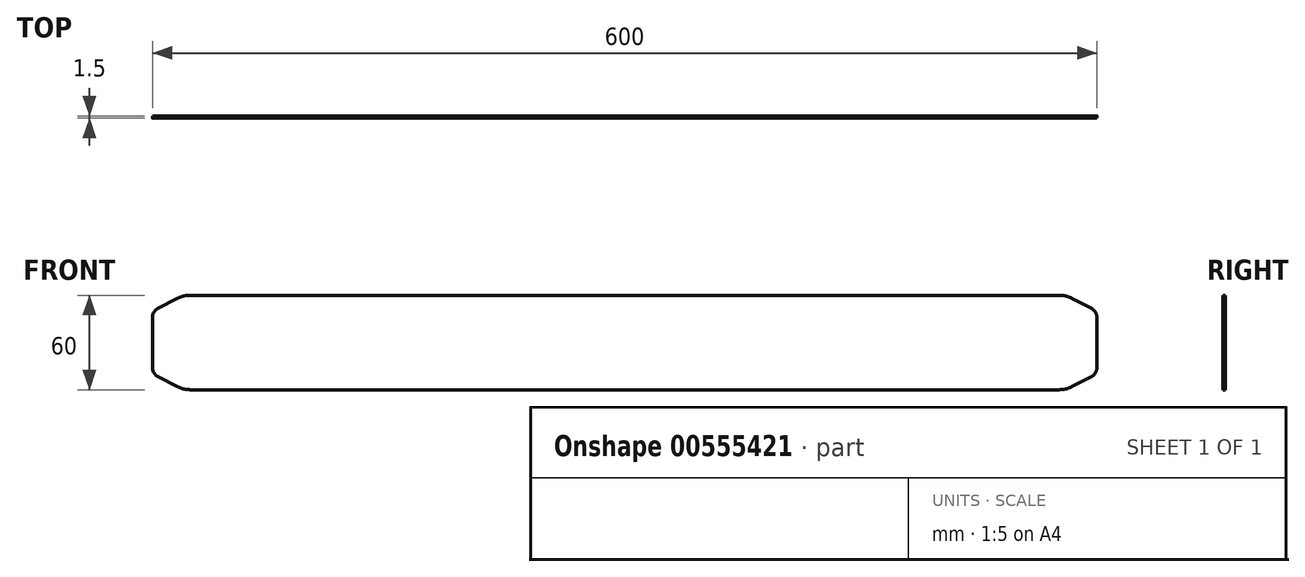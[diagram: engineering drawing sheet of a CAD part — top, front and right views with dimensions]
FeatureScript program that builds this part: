
annotation { "Feature Type Name" : "Feature", "Feature Type Description" : "" }
export const myFeature = defineFeature(function(context is Context, id is Id, definition is map)
    precondition{}
    {
        {
            var Q0;
            Q0=qCreatedBy(makeId("Front.planeOp"),FACE);
            var sketch = newSketch(context, id + "F0", { "sketchPlane" : qUnion([Q0])});
            skLineSegment(sketch, "E0", {"start": v(-284.17, 28.04) * mm, "end": v(-296.18, 21.92) * mm});
            skLineSegment(sketch, "E1", {"start": v(-300, 15.68) * mm, "end": v(-300, 0) * mm});
            skLineSegment(sketch, "E2", {"start": v(-300, 0) * mm, "end": v(0, 0) * mm, "construction": true});
            skLineSegment(sketch, "E3", {"start": v(-276, 30) * mm, "end": v(0, 30) * mm});
            skLineSegment(sketch, "E4", {"start": v(0, 30) * mm, "end": v(0, 0) * mm, "construction": true});
            skPoint(sketch, "E5.visualSharp", {"position": v(-280.32, 30) * mm});
            skArc(sketch, "E5.filletArc", {"start": v(-276, 30) * mm, "mid": v(-280.2, 29.5) * mm, "end": v(-284.17, 28.04) * mm});
            skPoint(sketch, "E6.visualSharp", {"position": v(-300, 19.97) * mm});
            skArc(sketch, "E6.filletArc", {"start": v(-296.18, 21.92) * mm, "mid": v(-298.97, 19.34) * mm, "end": v(-300, 15.68) * mm});
            skLineSegment(sketch, "E7.MirrorCS", {"start": v(-300, -15.68) * mm, "end": v(-300, 0) * mm});
            skArc(sketch, "E8.MirrorCS", {"start": v(-296.18, -21.92) * mm, "mid": v(-298.97, -19.34) * mm, "end": v(-300, -15.68) * mm});
            skLineSegment(sketch, "E9.MirrorCS", {"start": v(-284.17, -28.04) * mm, "end": v(-296.18, -21.92) * mm});
            skLineSegment(sketch, "E10.MirrorCS", {"start": v(-276, -30) * mm, "end": v(0, -30) * mm});
            skArc(sketch, "E11.MirrorCS", {"start": v(-276, -30) * mm, "mid": v(-280.2, -29.5) * mm, "end": v(-284.17, -28.04) * mm});
            skLineSegment(sketch, "E12.MirrorCS", {"start": v(276, 30) * mm, "end": v(0, 30) * mm});
            skLineSegment(sketch, "E13.MirrorCS", {"start": v(276, -30) * mm, "end": v(0, -30) * mm});
            skLineSegment(sketch, "E14.MirrorCS", {"start": v(300, -15.68) * mm, "end": v(300, 0) * mm});
            skLineSegment(sketch, "E15.MirrorCS", {"start": v(300, 15.68) * mm, "end": v(300, 0) * mm});
            skPoint(sketch, "E16.MirrorP", {"position": v(300, 19.97) * mm});
            skArc(sketch, "E17.MirrorCS", {"start": v(296.18, 21.92) * mm, "mid": v(298.97, 19.34) * mm, "end": v(300, 15.68) * mm});
            skLineSegment(sketch, "E18.MirrorCS", {"start": v(284.17, 28.04) * mm, "end": v(296.18, 21.92) * mm});
            skArc(sketch, "E19.MirrorCS", {"start": v(276, 30) * mm, "mid": v(280.2, 29.5) * mm, "end": v(284.17, 28.04) * mm});
            skArc(sketch, "E20.MirrorCS", {"start": v(276, -30) * mm, "mid": v(280.2, -29.5) * mm, "end": v(284.17, -28.04) * mm});
            skLineSegment(sketch, "E21.MirrorCS", {"start": v(284.17, -28.04) * mm, "end": v(296.18, -21.92) * mm});
            skArc(sketch, "E22.MirrorCS", {"start": v(296.18, -21.92) * mm, "mid": v(298.97, -19.34) * mm, "end": v(300, -15.68) * mm});
            skSolve(sketch);
        }
        {
            var Q0;
            Q0=makeQuery(id+"F0.imprint","IMPRINT",FACE,{"disambiguationData":[TD([[makeQuery(id+"F0.imprint","IMPRINT",EDGE,{"derivedFrom":sQuery(id+"F0.wireOp",EDGE,"E0")}),1.0]])]});
            extrude(context, id + "F1", {"entities" : qUnion([Q0]), "depth" : 1.5 * mm, "offsetDistance" : 25 * mm});
        }
    });
